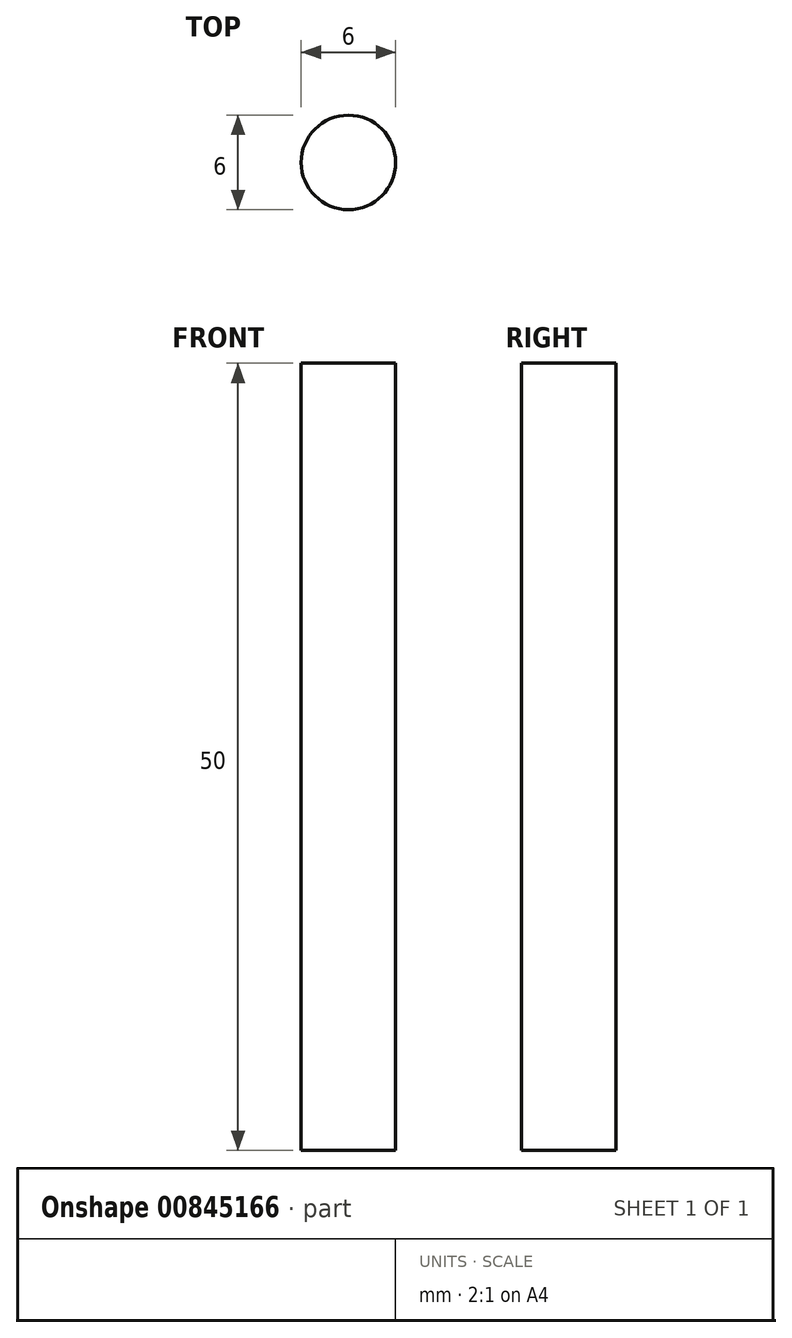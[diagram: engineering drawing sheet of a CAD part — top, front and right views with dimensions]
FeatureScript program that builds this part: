
annotation { "Feature Type Name" : "Feature", "Feature Type Description" : "" }
export const myFeature = defineFeature(function(context is Context, id is Id, definition is map)
    precondition{}
    {
        {
            var Q0;
            Q0=qCreatedBy(makeId("Top.planeOp"),FACE);
            var sketch = newSketch(context, id + "F0", { "sketchPlane" : qUnion([Q0])});
            skCircle(sketch, "E0", {"center": v(0, 0) * mm, "radius": 3 * mm});
            skSolve(sketch);
        }
        {
            var Q0;
            Q0 = qSketchRegion(id + "F0", true);
            extrude(context, id + "F1", {"entities" : qUnion([Q0]), "depth" : 50 * mm, "offsetDistance" : 25 * mm});
        }
    });
